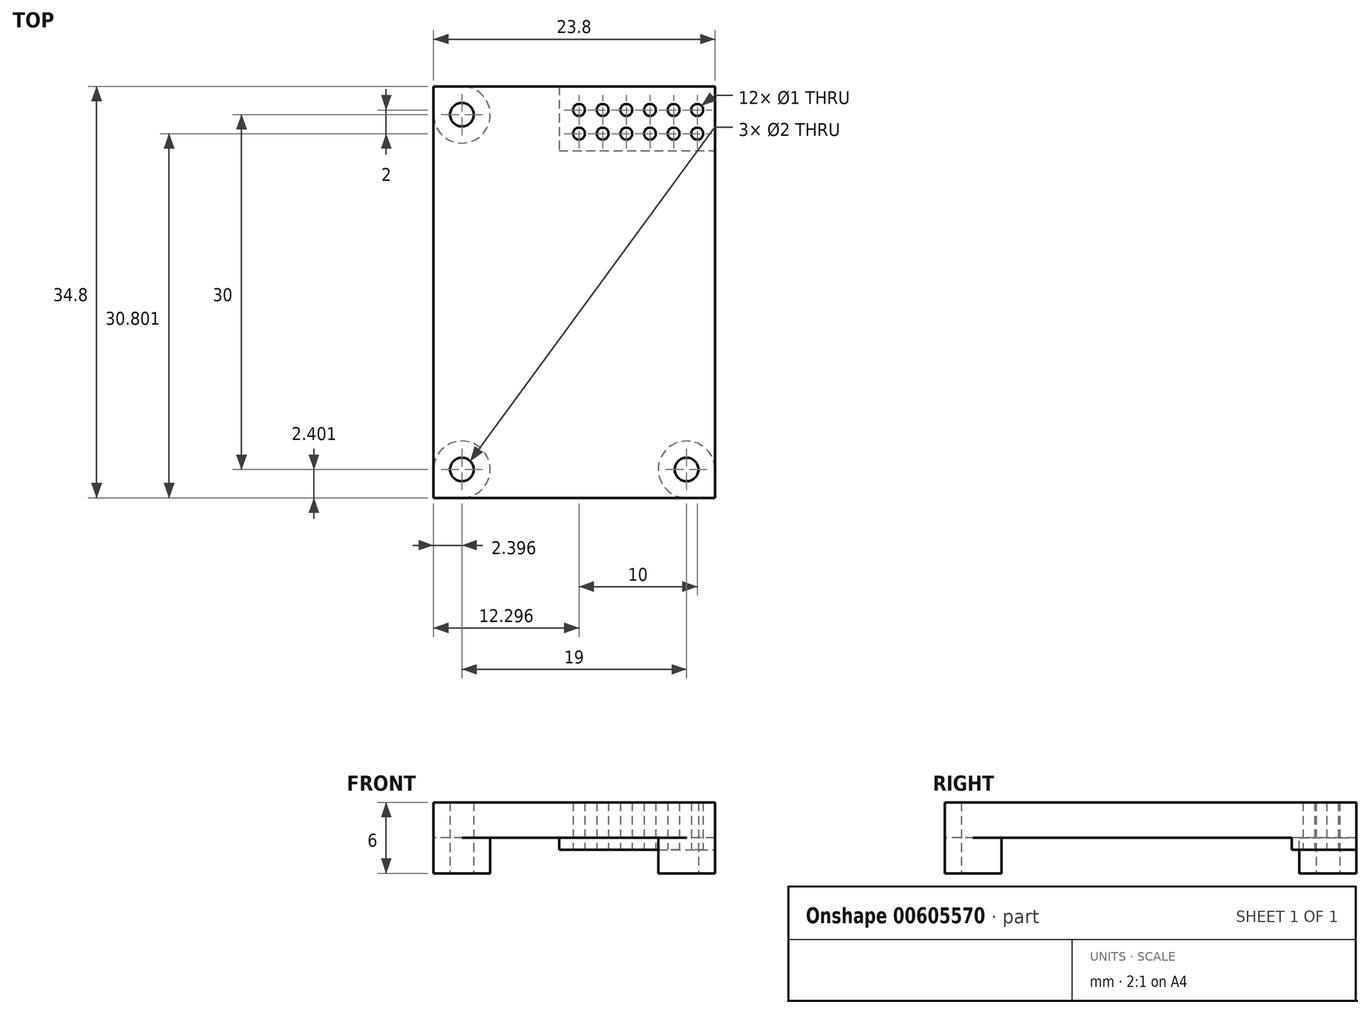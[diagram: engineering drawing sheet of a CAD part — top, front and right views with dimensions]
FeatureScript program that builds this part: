
annotation { "Feature Type Name" : "Feature", "Feature Type Description" : "" }
export const myFeature = defineFeature(function(context is Context, id is Id, definition is map)
    precondition{}
    {
        {
            var Q0;
            Q0=qCreatedBy(makeId("Top.planeOp"),FACE);
            var sketch = newSketch(context, id + "F0", { "sketchPlane" : qUnion([Q0])});
            skLineSegment(sketch, "E0.bottom", {"start": v(-2.78, 3.21) * mm, "end": v(21.02, 3.21) * mm});
            skLineSegment(sketch, "E0.top", {"start": v(-2.78, -31.59) * mm, "end": v(21.02, -31.59) * mm});
            skLineSegment(sketch, "E0.left", {"start": v(-2.78, 3.21) * mm, "end": v(-2.78, -31.59) * mm});
            skLineSegment(sketch, "E0.right", {"start": v(21.02, 3.21) * mm, "end": v(21.02, -31.59) * mm});
            skLineSegment(sketch, "E1", {"start": v(8.52, 3.21) * mm, "end": v(8.52, -1.29) * mm, "construction": true});
            skLineSegment(sketch, "E2", {"start": v(8.52, -1.29) * mm, "end": v(21.02, -1.29) * mm, "construction": true});
            skCircle(sketch, "E3", {"center": v(9.52, -0.79) * mm, "radius": 0.5 * mm});
            skCircle(sketch, "E4.1.0.0", {"center": v(11.52, -0.79) * mm, "radius": 0.5 * mm});
            skCircle(sketch, "E4.2.0.0", {"center": v(13.52, -0.79) * mm, "radius": 0.5 * mm});
            skCircle(sketch, "E4.3.0.0", {"center": v(15.52, -0.79) * mm, "radius": 0.5 * mm});
            skCircle(sketch, "E4.4.0.0", {"center": v(17.52, -0.79) * mm, "radius": 0.5 * mm});
            skCircle(sketch, "E4.5.0.0", {"center": v(19.52, -0.79) * mm, "radius": 0.5 * mm});
            skLineSegment(sketch, "E4.direction1", {"start": v(9.52, -0.79) * mm, "end": v(11.52, -0.79) * mm, "construction": true});
            skLineSegment(sketch, "E5", {"start": v(8.93, 0.21) * mm, "end": v(19.83, 0.21) * mm, "construction": true});
            skCircle(sketch, "E6.MirrorC", {"center": v(9.52, 1.21) * mm, "radius": 0.5 * mm});
            skCircle(sketch, "E7.MirrorC", {"center": v(11.52, 1.21) * mm, "radius": 0.5 * mm});
            skCircle(sketch, "E8.MirrorC", {"center": v(13.52, 1.21) * mm, "radius": 0.5 * mm});
            skCircle(sketch, "E9.MirrorC", {"center": v(15.52, 1.21) * mm, "radius": 0.5 * mm});
            skCircle(sketch, "E10.MirrorC", {"center": v(17.52, 1.21) * mm, "radius": 0.5 * mm});
            skCircle(sketch, "E11.MirrorC", {"center": v(19.52, 1.21) * mm, "radius": 0.5 * mm});
            skLineSegment(sketch, "E12", {"start": v(-2.78, -14.19) * mm, "end": v(21.02, -14.19) * mm, "construction": true});
            skLineSegment(sketch, "E13", {"start": v(9.12, -31.59) * mm, "end": v(9.12, 3.21) * mm, "construction": true});
            skLineSegment(sketch, "E14.bottom", {"start": v(-0.38, 0.81) * mm, "end": v(18.62, 0.81) * mm, "construction": true});
            skLineSegment(sketch, "E14.top", {"start": v(-0.38, -29.19) * mm, "end": v(18.62, -29.19) * mm, "construction": true});
            skLineSegment(sketch, "E14.left", {"start": v(-0.38, 0.81) * mm, "end": v(-0.38, -29.19) * mm, "construction": true});
            skLineSegment(sketch, "E14.right", {"start": v(18.62, 0.81) * mm, "end": v(18.62, -29.19) * mm, "construction": true});
            skPoint(sketch, "E14.middle", {"position": v(9.12, -14.19) * mm});
            skCircle(sketch, "E15", {"center": v(-0.38, 0.81) * mm, "radius": 1 * mm});
            skCircle(sketch, "E16", {"center": v(-0.38, -29.19) * mm, "radius": 1 * mm});
            skCircle(sketch, "E17", {"center": v(18.62, -29.19) * mm, "radius": 1 * mm});
            skSolve(sketch);
        }
        {
            var Q0;
            Q0 = qSketchRegion(id + "F0", true);
            extrude(context, id + "F1", {"entities" : qUnion([Q0]), "depth" : 3 * mm, "offsetDistance" : 25 * mm});
        }
        {
            var Q0;
            Q0=makeQuery(id+"F1.opExtrude","CAP_FACE",FACE,{"disambiguationData":[OSD([sQuery(id+"F0.wireOp",EDGE,"E0.bottom"),sQuery(id+"F0.wireOp",EDGE,"E0.top"),sQuery(id+"F0.wireOp",EDGE,"E0.left"),sQuery(id+"F0.wireOp",EDGE,"E0.right"),sQuery(id+"F0.wireOp",EDGE,"E3"),sQuery(id+"F0.wireOp",EDGE,"E4.1.0.0"),sQuery(id+"F0.wireOp",EDGE,"E4.2.0.0"),sQuery(id+"F0.wireOp",EDGE,"E4.3.0.0"),sQuery(id+"F0.wireOp",EDGE,"E4.4.0.0"),sQuery(id+"F0.wireOp",EDGE,"E4.5.0.0"),sQuery(id+"F0.wireOp",EDGE,"E6.MirrorC"),sQuery(id+"F0.wireOp",EDGE,"E7.MirrorC"),sQuery(id+"F0.wireOp",EDGE,"E8.MirrorC"),sQuery(id+"F0.wireOp",EDGE,"E9.MirrorC"),sQuery(id+"F0.wireOp",EDGE,"E10.MirrorC"),sQuery(id+"F0.wireOp",EDGE,"E11.MirrorC"),sQuery(id+"F0.wireOp",EDGE,"E15"),sQuery(id+"F0.wireOp",EDGE,"E16"),sQuery(id+"F0.wireOp",EDGE,"E17")])],"isStart":false});
            var sketch = newSketch(context, id + "F2", { "sketchPlane" : qUnion([Q0])});
            skCircle(sketch, "E18.0", {"center": v(9.52, -0.79) * mm, "radius": 0.5 * mm});
            skCircle(sketch, "E18.1", {"center": v(9.52, 1.21) * mm, "radius": 0.5 * mm});
            skCircle(sketch, "E18.2", {"center": v(11.52, 1.21) * mm, "radius": 0.5 * mm});
            skCircle(sketch, "E18.3", {"center": v(11.52, -0.79) * mm, "radius": 0.5 * mm});
            skCircle(sketch, "E18.4", {"center": v(13.52, -0.79) * mm, "radius": 0.5 * mm});
            skCircle(sketch, "E18.5", {"center": v(13.52, 1.21) * mm, "radius": 0.5 * mm});
            skCircle(sketch, "E18.6", {"center": v(15.52, 1.21) * mm, "radius": 0.5 * mm});
            skCircle(sketch, "E18.7", {"center": v(15.52, -0.79) * mm, "radius": 0.5 * mm});
            skCircle(sketch, "E18.8", {"center": v(17.52, -0.79) * mm, "radius": 0.5 * mm});
            skCircle(sketch, "E18.9", {"center": v(17.52, 1.21) * mm, "radius": 0.5 * mm});
            skCircle(sketch, "E18.10", {"center": v(19.52, 1.21) * mm, "radius": 0.5 * mm});
            skCircle(sketch, "E18.11", {"center": v(19.52, -0.79) * mm, "radius": 0.5 * mm});
            skCircle(sketch, "E18.12", {"center": v(-0.38, 0.81) * mm, "radius": 1 * mm});
            skCircle(sketch, "E18.13", {"center": v(-0.38, -29.19) * mm, "radius": 1 * mm});
            skCircle(sketch, "E18.14", {"center": v(18.62, -29.19) * mm, "radius": 1 * mm});
            skLineSegment(sketch, "E19.0", {"start": v(-2.78, 3.21) * mm, "end": v(21.02, 3.21) * mm});
            skLineSegment(sketch, "E19.1", {"start": v(21.02, 3.21) * mm, "end": v(21.02, -31.59) * mm});
            skLineSegment(sketch, "E20", {"start": v(7.84, 3.21) * mm, "end": v(7.84, -2.24) * mm});
            skLineSegment(sketch, "E21", {"start": v(7.84, -2.24) * mm, "end": v(21.02, -2.24) * mm});
            skCircle(sketch, "E22", {"center": v(-0.38, 0.81) * mm, "radius": 2.4 * mm});
            skCircle(sketch, "E23", {"center": v(-0.38, -29.19) * mm, "radius": 2.4 * mm});
            skCircle(sketch, "E24", {"center": v(18.62, -29.19) * mm, "radius": 2.4 * mm});
            skSolve(sketch);
        }
        {
            var Q0;
            Q0=makeQuery(id+"F2.imprint","IMPRINT",FACE,{"disambiguationData":[TD([[makeQuery(id+"F2.imprint","IMPRINT",EDGE,{"derivedFrom":sQuery(id+"F2.wireOp",EDGE,"E18.0")}),-1.0]])]});
            extrude(context, id + "F3", {"entities" : qUnion([Q0]), "operationType" : NewBodyOperationType.ADD, "oppositeDirection" : true, "depth" : 4 * mm, "offsetDistance" : 25 * mm});
        }
        {
            var Q0;
            Q0=makeQuery(id+"F2.imprint","IMPRINT",FACE,{"disambiguationData":[TD([[makeQuery(id+"F2.imprint","IMPRINT",EDGE,{"derivedFrom":sQuery(id+"F2.wireOp",EDGE,"E18.12")}),-1.0]])]});
            var Q1;
            Q1=makeQuery(id+"F2.imprint","IMPRINT",FACE,{"disambiguationData":[TD([[makeQuery(id+"F2.imprint","IMPRINT",EDGE,{"derivedFrom":sQuery(id+"F2.wireOp",EDGE,"E18.13")}),-1.0]])]});
            var Q2;
            Q2=makeQuery(id+"F2.imprint","IMPRINT",FACE,{"disambiguationData":[TD([[makeQuery(id+"F2.imprint","IMPRINT",EDGE,{"derivedFrom":sQuery(id+"F2.wireOp",EDGE,"E18.14")}),-1.0]])]});
            var Q3;
            {var subQ0=sQuery(id+"F2.wireOp",EDGE,"E19.1");var subQ1=makeQuery(id+"F1.opExtrude","CAP_EDGE",EDGE,{"disambiguationData":[OSD([sQuery(id+"F0.wireOp",EDGE,"E0.top")])],"isStart":false});var subQ2=makeQuery(id+"F2.imprint","INTERSECT",VERTEX,{"derivedFrom":[subQ1,subQ0]});Q3=makeQuery(id+"F2.imprint","IMPRINT",FACE,{"disambiguationData":[TD([[makeQuery(id+"F2.imprint","IMPRINT",EDGE,{"disambiguationData":[TD([[subQ2,1.0]])],"derivedFrom":subQ0}),-1.0]])]});}
            var Q4;
            {var subQ0=sQuery(id+"F2.wireOp",EDGE,"E23");var subQ1=makeQuery(id+"F1.opExtrude","CAP_EDGE",EDGE,{"disambiguationData":[OSD([sQuery(id+"F0.wireOp",EDGE,"E0.top")])],"isStart":false});var subQ2=makeQuery(id+"F2.imprint","INTERSECT",VERTEX,{"derivedFrom":[subQ1,subQ0]});Q4=makeQuery(id+"F2.imprint","IMPRINT",FACE,{"disambiguationData":[TD([[makeQuery(id+"F2.imprint","IMPRINT",EDGE,{"disambiguationData":[TD([[subQ2,1.0]])],"derivedFrom":subQ0}),-1.0]])]});}
            var Q5;
            {var subQ0=sQuery(id+"F2.wireOp",EDGE,"E19.0");var subQ1=makeQuery(id+"F1.opExtrude","CAP_EDGE",EDGE,{"disambiguationData":[OSD([sQuery(id+"F0.wireOp",EDGE,"E0.left")])],"isStart":false});var subQ2=makeQuery(id+"F2.imprint","INTERSECT",VERTEX,{"derivedFrom":[subQ1,subQ0]});Q5=makeQuery(id+"F2.imprint","IMPRINT",FACE,{"disambiguationData":[TD([[makeQuery(id+"F2.imprint","IMPRINT",EDGE,{"disambiguationData":[TD([[subQ2,-1.0]])],"derivedFrom":subQ0}),-1.0]])]});}
            extrude(context, id + "F4", {"entities" : qUnion([Q0, Q1, Q2, Q3, Q4, Q5]), "operationType" : NewBodyOperationType.ADD, "oppositeDirection" : true, "depth" : 6 * mm, "offsetDistance" : 25 * mm});
        }
    });
